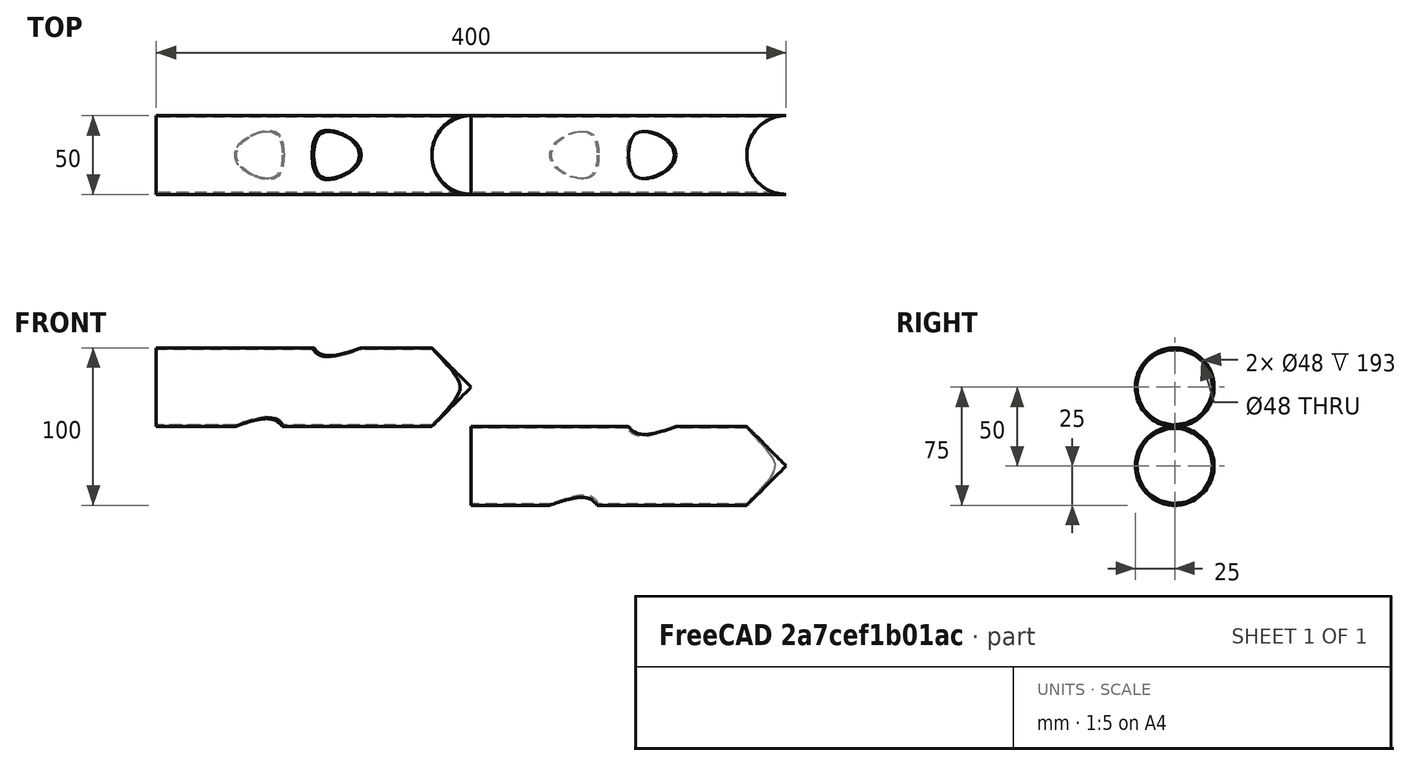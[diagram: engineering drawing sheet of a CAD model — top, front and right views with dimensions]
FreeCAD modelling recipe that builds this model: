
FCSTD DOCUMENT  (FreeCAD 0.20R26075 +2 (Git))
Label: pipe_normalcut_test
License: All rights reserved
LicenseURL: http://en.wikipedia.org/wiki/All_rights_reserved
objects: Part::FeaturePython×4, App::Link×2, Part::Offset×2, Part::Feature×2, Part::Cylinder×1, Part::MultiCommon×1, App::DocumentObjectGroup×1
note: 10 computed .brp shape members not serialized (recipe doc carries the construction recipe); baked Part::Feature solids carry a one-line shape summary decoded from their .brp

FEATURE [Part::Cylinder] Cylinder
  Angle = 360
  AttacherType = Attacher::AttachEngine3D
  FirstAngle = 45
  Height = 80
  Placement = pos=(-150,0,10) rot=(0,0,1;0rad)
  Radius = 15
  SecondAngle = 0
FEATURE [Part::FeaturePython] Tube  # WARN: FeaturePython — macro-defined, semantics opaque (R4)
  AttacherType = Attacher::AttachEngine3D
  Height = 100
  InnerRadius = 24
  OuterRadius = 25
FEATURE [Part::FeaturePython] Tube001  # WARN: FeaturePython — macro-defined, semantics opaque (R4)
  AttacherType = Attacher::AttachEngine3D
  Height = 200
  InnerRadius = 24
  OuterRadius = 25
  Placement = pos=(0,0,50) rot=(0.357407,-0.862856,-0.357407;1.71777rad)
FEATURE [Part::FeaturePython] Cutout  # WARN: FeaturePython — macro-defined, semantics opaque (R4)
  Base = -> Tube001
  Tolerance = 0
  Tool = -> Tube
FEATURE [Part::FeaturePython] Cutout001  # WARN: FeaturePython — macro-defined, semantics opaque (R4)
  Base = -> Cutout
  Tolerance = 0
  Tool = -> Cylinder
FEATURE [App::Link] Link  label="Cutout002"
  LinkTransform = true
  LinkedObject = -> Cutout001 [Face1]
FEATURE [App::Link] Link001  label="Cutout003"
  LinkTransform = true
  LinkedObject = -> Cutout001 [Face6]
FEATURE [Part::Offset] Offset
  Fill = true
  Intersection = false
  Join = 0
  Mode = 0
  SelfIntersection = false
  Source = -> Link
  Value = -1
FEATURE [Part::Offset] Offset001
  Fill = true
  Intersection = false
  Join = 0
  Mode = 0
  SelfIntersection = false
  Source = -> Link001
  Value = -1
FEATURE [Part::MultiCommon] Common
  Shapes = -> [Offset,Offset001]
FEATURE [App::DocumentObjectGroup] Group  label="Model"
  Group = -> [Cutout001,Common]
FEATURE [Part::Feature] Cutout001001
  Placement = pos=(200,0,-50) rot=(0,0,1;0rad)
  shape: bbox 200 x 50 x 50 mm, 6 faces (baked)
FEATURE [Part::Feature] Normals
  shape: bbox 200 x 60 x 60 mm, 0 faces, 0 solids (baked)
